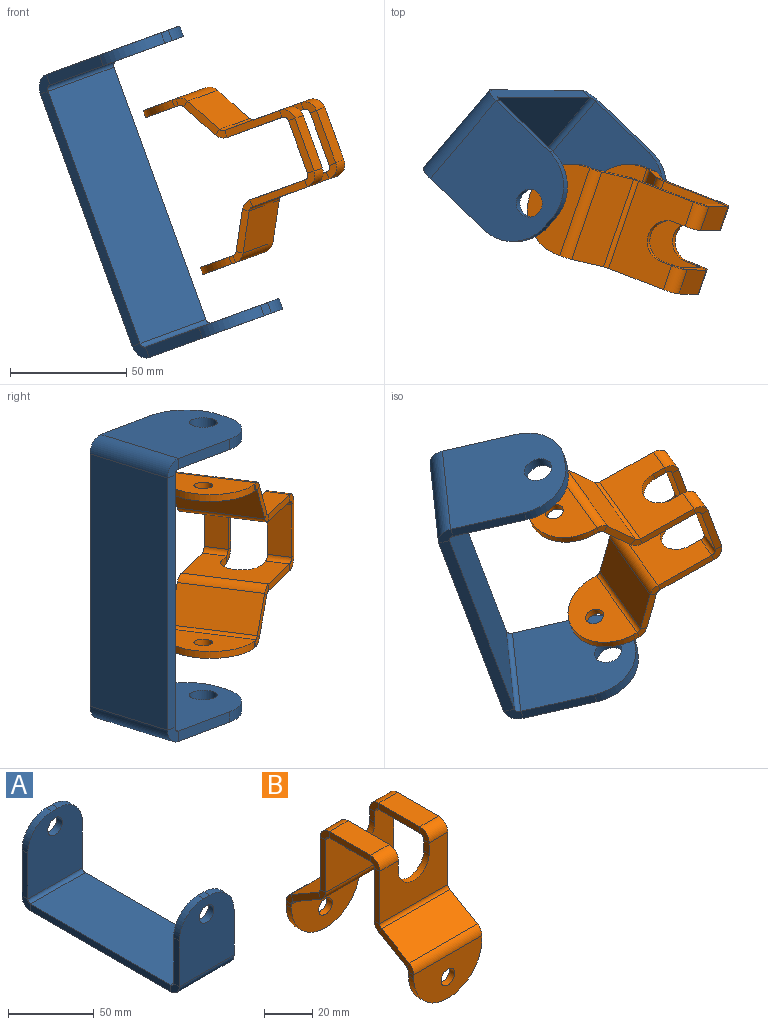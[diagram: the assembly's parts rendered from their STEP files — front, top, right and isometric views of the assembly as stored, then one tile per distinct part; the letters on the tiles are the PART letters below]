
ASSEMBLY  parts=2 mates=1
PART A: 28 faces, bbox 45x129.5x59.8 mm
  f0: plane 32.71x4.75mm, normal (-1,0,0), area 155.4mm2, adj f4,f5,f7,f25
  f1: plane 32.71x4.75mm, normal (1,0,0), area 155.4mm2, adj f4,f5,f6,f24
  f2: cylinder r=6mm len=12mm, axis (0,-1,0), area 179.1mm2, adj f4,f5
  f3: plane 5x4.75mm, normal (0,0,1), area 23.8mm2, adj f4,f5,f6,f7
  f4: plane 52.71x45mm, normal (0,-1,0), area 2087.4mm2, adj f0,f1,f2,f3,f6,f7,f26
  f5: plane 52.71x45mm, normal (0,1,0), area 2087.4mm2, adj f0,f1,f2,f3,f6,f7,f27
  f6: cylinder r=20mm len=20mm, axis (0,-1,0), area 149.2mm2, adj f1,f3,f4,f5
  f7: cylinder r=20mm len=20mm, axis (0,1,0), area 149.2mm2, adj f0,f3,f4,f5
  f8: plane 115.43x4.75mm, normal (-1,0,0), area 548.3mm2, adj f10,f11,f21,f25
  f9: plane 115.43x4.75mm, normal (1,0,0), area 548.3mm2, adj f10,f11,f20,f24
  f10: plane 115.43x45mm, normal (0,0,-1), area 5194.3mm2, adj f8,f9,f22,f26
  f11: plane 115.43x45mm, normal (0,0,1), area 5194.3mm2, adj f8,f9,f23,f27
  f12: plane 32.71x4.75mm, normal (-1,0,0), area 155.4mm2, adj f16,f17,f18,f21
  f13: plane 5x4.75mm, normal (0,0,1), area 23.8mm2, adj f16,f17,f18,f19
  f14: plane 32.71x4.75mm, normal (1,0,0), area 155.4mm2, adj f16,f17,f19,f20
  f15: cylinder r=6mm len=12mm, axis (0,1,0), area 179.1mm2, adj f16,f17
  f16: plane 52.71x45mm, normal (0,1,0), area 2087.4mm2, adj f12,f13,f14,f15,f18,f19,f22
  f17: plane 52.71x45mm, normal (0,-1,0), area 2087.4mm2, adj f12,f13,f14,f15,f18,f19,f23
  f18: cylinder r=20mm len=20mm, axis (0,1,0), area 149.2mm2, adj f12,f13,f16,f17
  f19: cylinder r=20mm len=20mm, axis (0,-1,0), area 149.2mm2, adj f13,f14,f16,f17
  f20: plane 7.04x7.04mm, normal (1,0,0), area 34.8mm2, adj f9,f14,f22,f23
  f21: plane 7.04x7.04mm, normal (-1,0,0), area 34.8mm2, adj f8,f12,f22,f23
  f22: cylinder r=7.04mm len=45mm, axis (1,0,0), area 497.3mm2, adj f10,f16,f20,f21
  f23: cylinder r=2.29mm len=45mm, axis (1,0,0), area 161.6mm2, adj f11,f17,f20,f21
  f24: plane 7.04x7.04mm, normal (1,0,0), area 34.8mm2, adj f1,f9,f26,f27
  f25: plane 7.04x7.04mm, normal (-1,0,0), area 34.8mm2, adj f0,f8,f26,f27
  f26: cylinder r=7.04mm len=45mm, axis (1,0,0), area 497.3mm2, adj f4,f10,f24,f25
  f27: cylinder r=2.29mm len=45mm, axis (1,0,0), area 161.6mm2, adj f5,f11,f24,f25
PART B: 74 faces, bbox 40x75x70 mm
  f0: plane 3.18x1.85mm, normal (-1,0,0), area 5.9mm2, adj f3,f4,f5,f71
  f1: plane 3.18x1.85mm, normal (1,0,0), area 5.9mm2, adj f3,f4,f5,f70
  f2: cylinder r=4mm len=8mm, axis (0,1,0), area 79.8mm2, adj f3,f4
  f3: plane 40x21.85mm, normal (0,1,0), area 651.9mm2, adj f0,f1,f2,f5,f73
  f4: plane 40x21.85mm, normal (0,-1,0), area 651.9mm2, adj f0,f1,f2,f5,f72
  f5: cylinder r=20mm len=40mm, axis (0,1,0), area 199.5mm2, adj f0,f1,f3,f4
  f6: plane 17.71x12.06mm, normal (-1,0,0), area 59.1mm2, adj f8,f9,f67,f71
  f7: plane 17.71x12.06mm, normal (1,0,0), area 59.1mm2, adj f8,f9,f66,f70
  f8: plane 40x16.13mm, normal (0,0.5,-0.87), area 744.9mm2, adj f6,f7,f68,f73
  f9: plane 40x16.13mm, normal (0,-0.5,0.87), area 744.9mm2, adj f6,f7,f69,f72
  f10: plane 26.67x3.18mm, normal (1,0,0), area 84.7mm2, adj f14,f15,f58,f66
  f11: plane 26.67x3.18mm, normal (-1,0,0), area 84.7mm2, adj f14,f15,f63,f67
  f12: plane 5.54x3.18mm, normal (1,0,0), area 17.6mm2, adj f14,f15,f16,f62
  f13: plane 5.54x3.18mm, normal (-1,0,0), area 17.6mm2, adj f14,f15,f16,f59
  f14: plane 40x26.67mm, normal (0,1,0), area 840mm2, adj f10,f11,f12,f13,f16,f61,f65,f68
  f15: plane 40x26.67mm, normal (0,-1,0), area 840mm2, adj f10,f11,f12,f13,f16,f60,f64,f69
  f16: cylinder r=9mm len=18mm, axis (0,1,0), area 89.8mm2, adj f12,f13,f14,f15
  f17: plane 24.08x3.18mm, normal (-1,0,0), area 76.4mm2, adj f19,f20,f51,f63
  f18: plane 24.08x3.18mm, normal (1,0,0), area 76.4mm2, adj f19,f20,f50,f62
  f19: plane 24.08x11mm, normal (0,0,-1), area 264.9mm2, adj f17,f18,f53,f65
  f20: plane 24.08x11mm, normal (0,0,1), area 264.9mm2, adj f17,f18,f52,f64
  f21: plane 24.08x3.18mm, normal (1,0,0), area 76.4mm2, adj f23,f24,f54,f58
  f22: plane 24.08x3.18mm, normal (-1,0,0), area 76.4mm2, adj f23,f24,f55,f59
  f23: plane 24.08x11mm, normal (0,0,-1), area 264.9mm2, adj f21,f22,f57,f61
  f24: plane 24.08x11mm, normal (0,0,1), area 264.9mm2, adj f21,f22,f56,f60
  f25: plane 5.54x3.18mm, normal (1,0,0), area 17.6mm2, adj f29,f30,f31,f50
  f26: plane 26.67x3.18mm, normal (-1,0,0), area 84.7mm2, adj f29,f30,f47,f51
  f27: plane 26.67x3.18mm, normal (1,0,0), area 84.7mm2, adj f29,f30,f46,f54
  f28: plane 5.54x3.18mm, normal (-1,0,0), area 17.6mm2, adj f29,f30,f31,f55
  f29: plane 40x26.67mm, normal (0,-1,0), area 840mm2, adj f25,f26,f27,f28,f31,f48,f53,f57
  f30: plane 40x26.67mm, normal (0,1,0), area 840mm2, adj f25,f26,f27,f28,f31,f49,f52,f56
  f31: cylinder r=9mm len=18mm, axis (0,-1,0), area 89.8mm2, adj f25,f28,f29,f30
  f32: plane 17.71x12.06mm, normal (-1,0,0), area 59.1mm2, adj f34,f35,f43,f47
  f33: plane 17.71x12.06mm, normal (1,0,0), area 59.1mm2, adj f34,f35,f42,f46
  f34: plane 40x16.13mm, normal (0,-0.5,-0.87), area 744.9mm2, adj f32,f33,f45,f48
  f35: plane 40x16.13mm, normal (0,0.5,0.87), area 744.9mm2, adj f32,f33,f44,f49
  f36: plane 3.18x1.85mm, normal (-1,0,0), area 5.9mm2, adj f39,f40,f41,f43
  f37: plane 3.18x1.85mm, normal (1,0,0), area 5.9mm2, adj f39,f40,f41,f42
  f38: cylinder r=4mm len=8mm, axis (0,-1,0), area 79.8mm2, adj f39,f40
  f39: plane 40x21.85mm, normal (0,-1,0), area 651.9mm2, adj f36,f37,f38,f41,f45
  f40: plane 40x21.85mm, normal (0,1,0), area 651.9mm2, adj f36,f37,f38,f41,f44
  f41: cylinder r=20mm len=40mm, axis (0,-1,0), area 199.5mm2, adj f36,f37,f39,f40
  f42: plane 4.73x4.32mm, normal (1,0,0), area 12.9mm2, adj f33,f37,f44,f45
  f43: plane 4.73x4.32mm, normal (-1,0,0), area 12.9mm2, adj f32,f36,f44,f45
  f44: cylinder r=5.46mm len=40mm, axis (1,0,0), area 228.7mm2, adj f35,f40,f42,f43
  f45: cylinder r=2.29mm len=40mm, axis (1,0,0), area 95.8mm2, adj f34,f39,f42,f43
  f46: plane 4.73x4.32mm, normal (1,0,0), area 12.9mm2, adj f27,f33,f48,f49
  f47: plane 4.73x4.32mm, normal (-1,0,0), area 12.9mm2, adj f26,f32,f48,f49
  f48: cylinder r=5.46mm len=40mm, axis (1,0,0), area 228.7mm2, adj f29,f34,f46,f47
  f49: cylinder r=2.29mm len=40mm, axis (1,0,0), area 95.8mm2, adj f30,f35,f46,f47
  f50: plane 5.46x5.46mm, normal (1,0,0), area 19.3mm2, adj f18,f25,f52,f53
  f51: plane 5.46x5.46mm, normal (-1,0,0), area 19.3mm2, adj f17,f26,f52,f53
  f52: cylinder r=5.46mm len=11mm, axis (1,0,0), area 94.4mm2, adj f20,f30,f50,f51
  f53: cylinder r=2.29mm len=11mm, axis (1,0,0), area 39.5mm2, adj f19,f29,f50,f51
  f54: plane 5.46x5.46mm, normal (1,0,0), area 19.3mm2, adj f21,f27,f56,f57
  f55: plane 5.46x5.46mm, normal (-1,0,0), area 19.3mm2, adj f22,f28,f56,f57
  f56: cylinder r=5.46mm len=11mm, axis (1,0,0), area 94.4mm2, adj f24,f30,f54,f55
  f57: cylinder r=2.29mm len=11mm, axis (1,0,0), area 39.5mm2, adj f23,f29,f54,f55
  f58: plane 5.46x5.46mm, normal (1,0,0), area 19.3mm2, adj f10,f21,f60,f61
  f59: plane 5.46x5.46mm, normal (-1,0,0), area 19.3mm2, adj f13,f22,f60,f61
  f60: cylinder r=5.46mm len=11mm, axis (1,0,0), area 94.4mm2, adj f15,f24,f58,f59
  f61: cylinder r=2.29mm len=11mm, axis (1,0,0), area 39.5mm2, adj f14,f23,f58,f59
  f62: plane 5.46x5.46mm, normal (1,0,0), area 19.3mm2, adj f12,f18,f64,f65
  f63: plane 5.46x5.46mm, normal (-1,0,0), area 19.3mm2, adj f11,f17,f64,f65
  f64: cylinder r=5.46mm len=11mm, axis (1,0,0), area 94.4mm2, adj f15,f20,f62,f63
  f65: cylinder r=2.29mm len=11mm, axis (1,0,0), area 39.5mm2, adj f14,f19,f62,f63
  f66: plane 4.73x4.32mm, normal (1,0,0), area 12.9mm2, adj f7,f10,f68,f69
  f67: plane 4.73x4.32mm, normal (-1,0,0), area 12.9mm2, adj f6,f11,f68,f69
  f68: cylinder r=5.46mm len=40mm, axis (1,0,0), area 228.7mm2, adj f8,f14,f66,f67
  f69: cylinder r=2.29mm len=40mm, axis (1,0,0), area 95.8mm2, adj f9,f15,f66,f67
  f70: plane 4.73x4.32mm, normal (1,0,0), area 12.9mm2, adj f1,f7,f72,f73
  f71: plane 4.73x4.32mm, normal (-1,0,0), area 12.9mm2, adj f0,f6,f72,f73
  f72: cylinder r=5.46mm len=40mm, axis (1,0,0), area 228.7mm2, adj f4,f9,f70,f71
  f73: cylinder r=2.29mm len=40mm, axis (1,0,0), area 95.8mm2, adj f3,f8,f70,f71
PLACE A rot(axis=(0.81,0.23,0.54),93.3deg) t=(-66.65,54.06,54.52)mm
PLACE B rot(axis=(0.65,0.39,0.65),100.3deg) t=(-45.72,28.93,60.46)mm
MATE cylindrical B.f2 <-> A.f2  axis (-0.34,0,0.94) through (-23.32,25.22,28.7)mm
